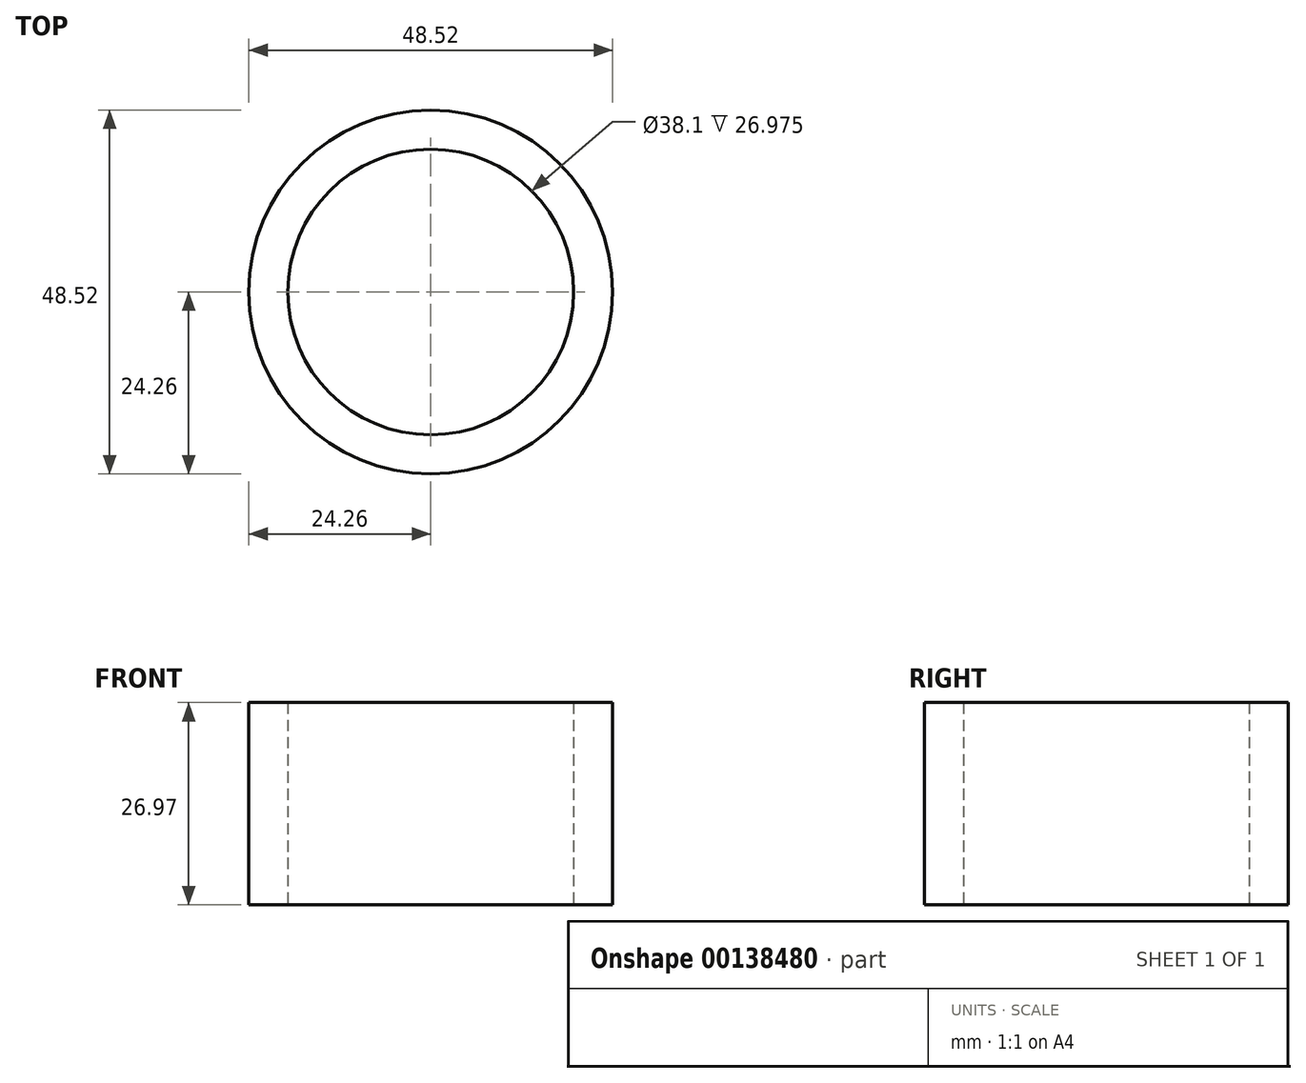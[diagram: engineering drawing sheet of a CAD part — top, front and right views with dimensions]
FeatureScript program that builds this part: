
annotation { "Feature Type Name" : "Feature", "Feature Type Description" : "" }
export const myFeature = defineFeature(function(context is Context, id is Id, definition is map)
    precondition{}
    {
        {
            var Q0;
            Q0=qCreatedBy(makeId("Top.planeOp"),FACE);
            var sketch = newSketch(context, id + "F0", { "sketchPlane" : qUnion([Q0])});
            skCircle(sketch, "E0", {"center": v(0, 0) * mm, "radius": 24.26 * mm});
            skCircle(sketch, "E1", {"center": v(0, 0) * mm, "radius": 19.05 * mm});
            skSolve(sketch);
        }
        {
            var Q0;
            Q0 = qSketchRegion(id + "F0", true);
            extrude(context, id + "F1", {"entities" : qUnion([Q0]), "depth" : 26.97 * mm});
        }
    });
